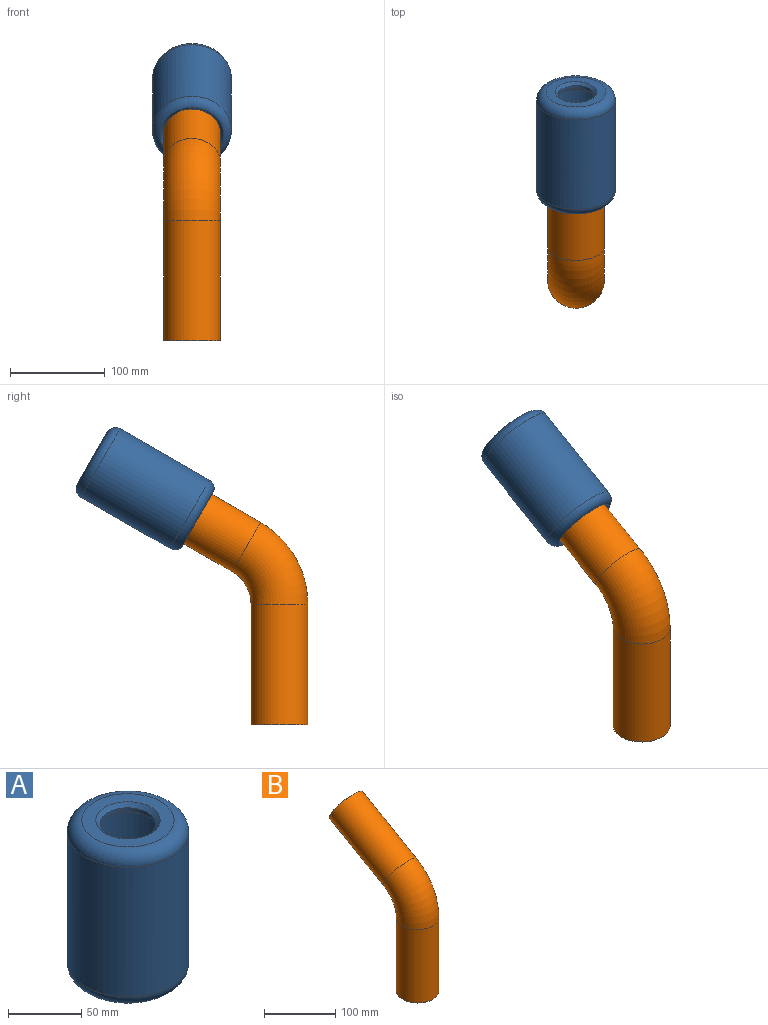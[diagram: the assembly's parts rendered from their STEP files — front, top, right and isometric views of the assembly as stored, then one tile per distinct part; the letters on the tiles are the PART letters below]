
ASSEMBLY  parts=2 mates=1
PART A: 12 faces, bbox 90x90x128.7 mm
  f0: plane 44.22x44.22mm, normal (0,0,-1), area 395.2mm2, adj f2,f9
  f1: cylinder r=32.11mm len=95.11mm, axis (0,0,-1), area 19189.5mm2, adj f2,f3
  f2: torus R=22.11mm, axis (0,0,-1), area 2810.6mm2, adj f0,f1
  f3: torus R=22.11mm, axis (0,0,1), area 1305.4mm2, adj f1,f4
  f4: cylinder r=30mm len=60mm, axis (0,0,-1), area 1528.8mm2, adj f3,f11
  f5: cylinder r=41.58mm len=108.68mm, axis (0,0,-1), area 28394.5mm2, adj f7,f8
  f6: plane 63.16x63.16mm, normal (0,0,1), area 1605mm2, adj f8,f10
  f7: torus R=31.58mm, axis (0,0,1), area 3326.8mm2, adj f5,f11
  f8: torus R=31.58mm, axis (0,0,-1), area 3745.2mm2, adj f5,f6
  f9: cylinder r=19.06mm len=38.11mm, axis (0,0,1), area 379.7mm2, adj f0,f10
  f10: cone r=19.06mm half-angle=45deg, axis (0,0,1), area 547.9mm2, adj f6,f9
  f11: cone r=30mm half-angle=50.9deg, axis (0,0,-1), area 929.8mm2, adj f4,f7
PART B: 8 faces, bbox 60x195.8x275.2 mm
  f0: cylinder r=28mm len=126.53mm, axis (0,0,1), area 22259.8mm2, adj f1,f3
  f1: torus R=70mm, axis (-1,0,0), area 12896.3mm2, adj f0,f2
  f2: cylinder r=28mm len=135.51mm, axis (0,0.87,0.5), area 21840.3mm2, adj f1,f4
  f3: plane 60x60mm, normal (0,0,-1), area 364.4mm2, adj f0,f5
  f4: plane 60x51.96mm, normal (0,0.87,0.5), area 364.4mm2, adj f2,f7
  f5: cylinder r=30mm len=126.53mm, axis (0,0,1), area 23849.7mm2, adj f3,f6
  f6: torus R=70mm, axis (-1,0,0), area 13817.4mm2, adj f5,f7
  f7: cylinder r=30mm len=137.51mm, axis (0,0.87,0.5), area 23400.4mm2, adj f4,f6
PLACE A rot(axis=(-1,0.03,0.05),60.1deg) t=(0,143.58,249.84)mm
PLACE B at identity fixed
MATE cylindrical B.f2 <-> A.f4  axis (0,0.87,0.5) through (0,88.76,218.18)mm
